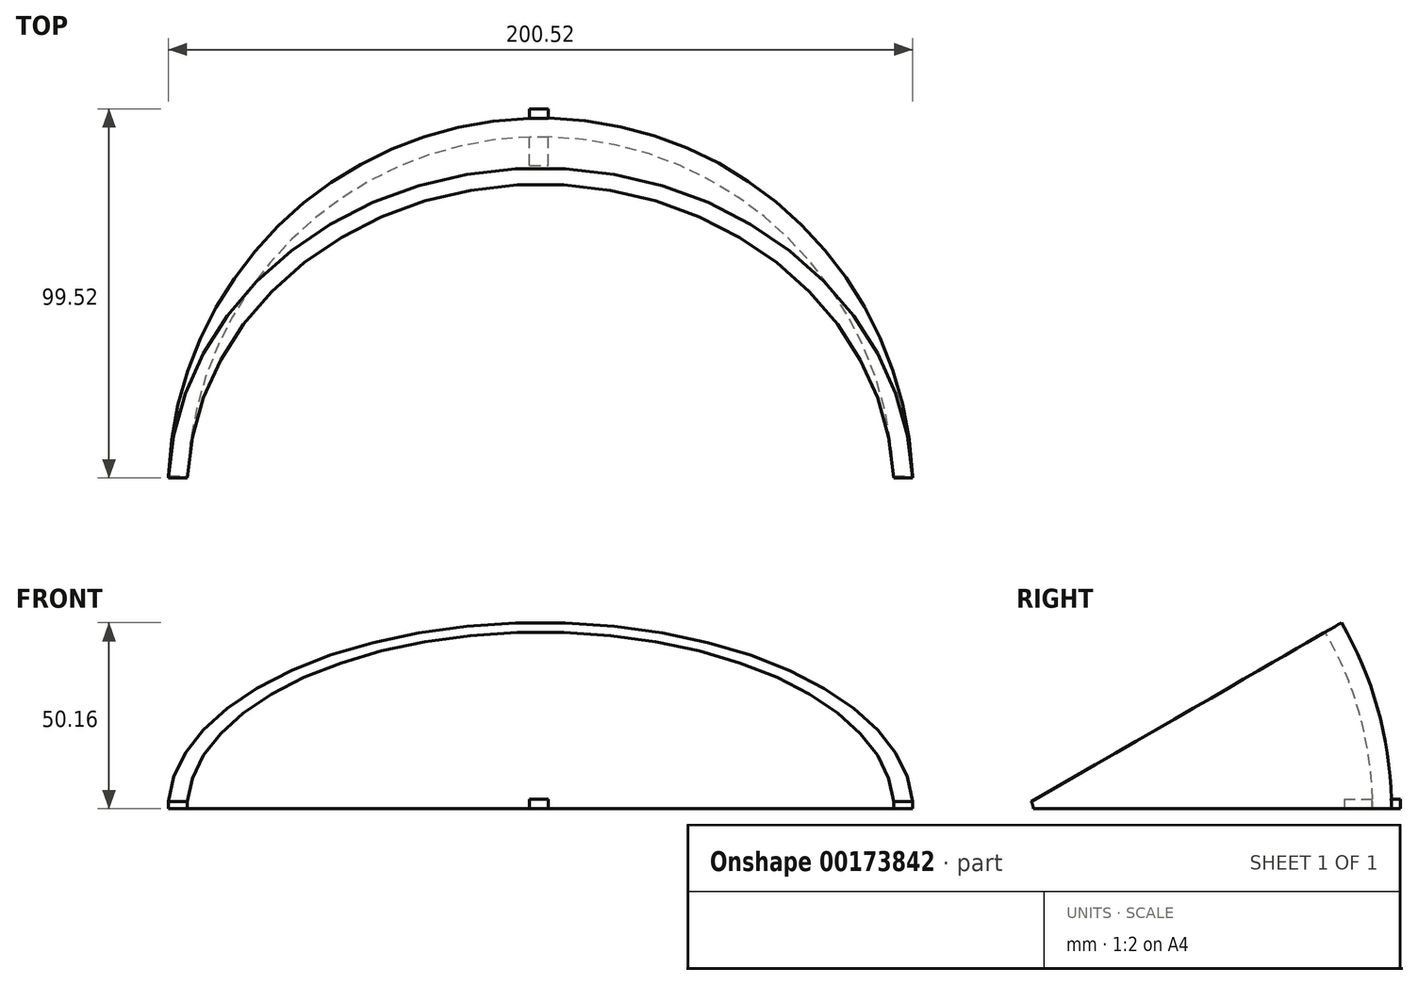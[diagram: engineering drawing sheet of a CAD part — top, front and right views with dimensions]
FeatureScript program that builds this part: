
annotation { "Feature Type Name" : "Feature", "Feature Type Description" : "" }
export const myFeature = defineFeature(function(context is Context, id is Id, definition is map)
    precondition{}
    {
        {
            var Q0;
            Q0=qCreatedBy(makeId("Top.planeOp"),FACE);
            var sketch = newSketch(context, id + "F0", { "sketchPlane" : qUnion([Q0])});
            skLineSegment(sketch, "E0", {"start": v(0, 0) * mm, "end": v(-95.25, 0) * mm, "construction": true});
            skArc(sketch, "E1", {"start": v(-95.25, 0) * mm, "mid": v(0, 95.25) * mm, "end": v(95.25, 0) * mm});
            skLineSegment(sketch, "E2", {"start": v(-95.25, 0) * mm, "end": v(-100.33, 0) * mm});
            skArc(sketch, "E3", {"start": v(-100.33, 0) * mm, "mid": v(0, 100.33) * mm, "end": v(100.33, 0) * mm});
            skLineSegment(sketch, "E4", {"start": v(95.25, 0) * mm, "end": v(100.33, 0) * mm});
            skSolve(sketch);
        }
        {
            var Q0;
            Q0=qSketchRegion(id+"F0",true);
            var Q1;
            Q1=sQuery(id+"F0.wireOp",EDGE,"E0");
            revolve(context, id + "F1", {"entities" : qUnion([Q0]), "axis" : qUnion([Q1]), "revolveType" : RevolveType.ONE_DIRECTION, "oppositeDirection" : true, "angle" : 30 * degree});
        }
        {
            var Q0;
            Q0=qCreatedBy(makeId("Right.planeOp"),FACE);
            var sketch = newSketch(context, id + "F2", { "sketchPlane" : qUnion([Q0])});
            skCircle(sketch, "E5", {"center": v(0, 0) * mm, "radius": 3.81 * mm});
            skSolve(sketch);
        }
        {
            var Q0;
            Q0=qSketchRegion(id+"F2",true);
            extrude(context, id + "F3", {"entities" : qUnion([Q0]), "operationType" : NewBodyOperationType.REMOVE, "endBound" : BoundingType.THROUGH_ALL, "oppositeDirection" : true, "depth" : 25.4 * mm, "hasSecondDirection" : true, "secondDirectionBound" : SecondDirectionBoundingType.THROUGH_ALL, "secondDirectionOppositeDirection" : false, "secondDirectionDepth" : 25.4 * mm});
        }
        {
            var Q0;
            Q0=qCreatedBy(makeId("Top.planeOp"),FACE);
            var sketch = newSketch(context, id + "F4", { "sketchPlane" : qUnion([Q0])});
            skLineSegment(sketch, "E6", {"start": v(0, 0) * mm, "end": v(2.54, 0) * mm, "construction": true});
            skLineSegment(sketch, "E7", {"start": v(0, 0) * mm, "end": v(-2.54, 0) * mm, "construction": true});
            skLineSegment(sketch, "E8", {"start": v(0, 0) * mm, "end": v(-95.25, 0) * mm, "construction": true});
            skArc(sketch, "E9", {"start": v(-95.25, 0) * mm, "mid": v(0, 95.25) * mm, "end": v(95.25, 0) * mm, "construction": true});
            skLineSegment(sketch, "E10", {"start": v(-2.93, 95.2) * mm, "end": v(-2.93, 102.82) * mm, "construction": true});
            skLineSegment(sketch, "E11", {"start": v(-2.93, 102.82) * mm, "end": v(2.15, 102.82) * mm});
            skLineSegment(sketch, "E12", {"start": v(-2.93, 95.2) * mm, "end": v(-2.93, 87.58) * mm, "construction": true});
            skLineSegment(sketch, "E13.bottom", {"start": v(-2.93, 87.58) * mm, "end": v(2.15, 87.58) * mm});
            skLineSegment(sketch, "E13.left", {"start": v(-2.93, 87.58) * mm, "end": v(-2.93, 102.82) * mm});
            skLineSegment(sketch, "E13.right", {"start": v(2.15, 87.58) * mm, "end": v(2.15, 102.82) * mm});
            skLineSegment(sketch, "E14", {"start": v(-2.93, 87.58) * mm, "end": v(-2.54, 0) * mm, "construction": true});
            skLineSegment(sketch, "E15", {"start": v(2.54, 0) * mm, "end": v(2.15, 95.23) * mm, "construction": true});
            skSolve(sketch);
        }
        {
            var Q0;
            Q0 = qSketchRegion(id + "F4", true);
            extrude(context, id + "F5", {"entities" : qUnion([Q0]), "operationType" : NewBodyOperationType.ADD, "depth" : 2.54 * mm});
        }
    });
